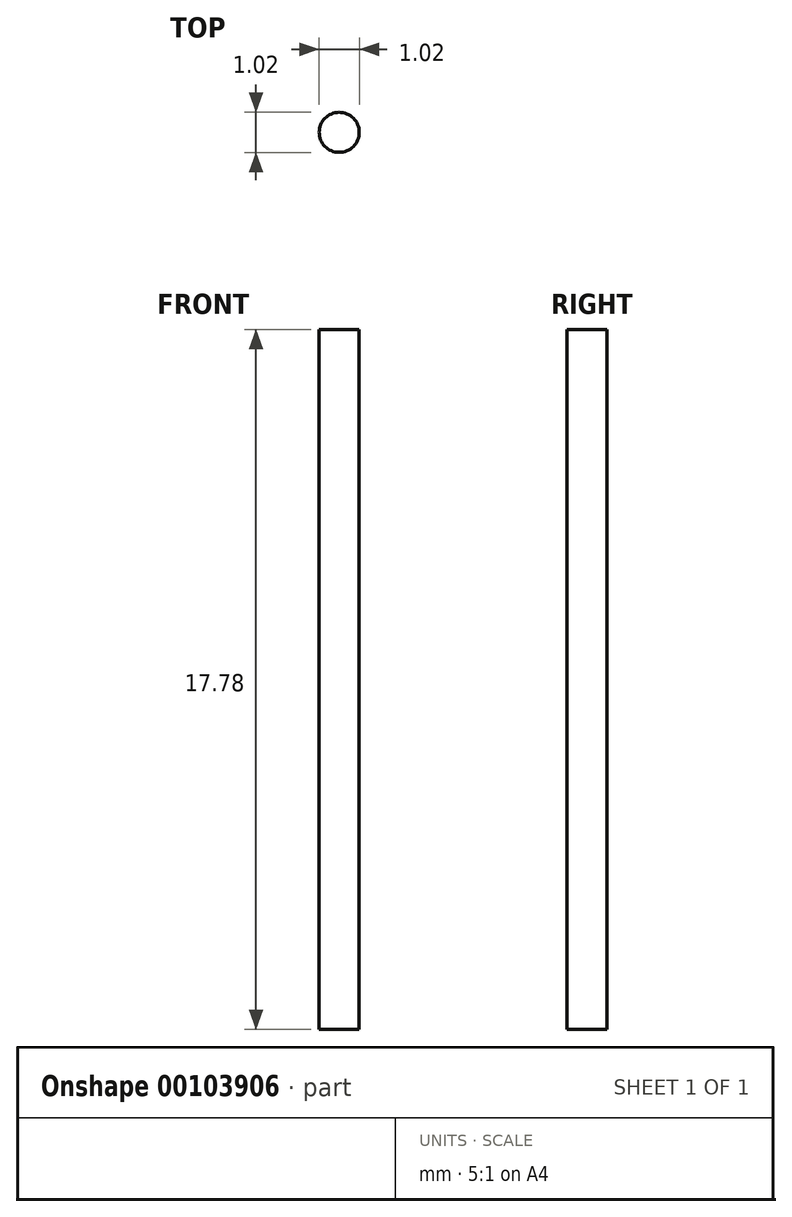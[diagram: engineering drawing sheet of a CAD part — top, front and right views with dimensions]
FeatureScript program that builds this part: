
annotation { "Feature Type Name" : "Feature", "Feature Type Description" : "" }
export const myFeature = defineFeature(function(context is Context, id is Id, definition is map)
    precondition{}
    {
        {
            var Q0;
            Q0=qCreatedBy(makeId("Top.planeOp"),FACE);
            var sketch = newSketch(context, id + "F0", { "sketchPlane" : qUnion([Q0])});
            skCircle(sketch, "E0", {"center": v(0, 0) * mm, "radius": 0.5 * mm});
            skSolve(sketch);
        }
        {
            var Q0;
            Q0=makeQuery(id+"F0.imprint","IMPRINT",FACE,{"disambiguationData":[TD([[makeQuery(id+"F0.imprint","IMPRINT",EDGE,{"derivedFrom":sQuery(id+"F0.wireOp",EDGE,"E0")}),1.0]])]});
            extrude(context, id + "F1", {"entities" : qUnion([Q0]), "depth" : 17.78 * mm});
        }
    });
